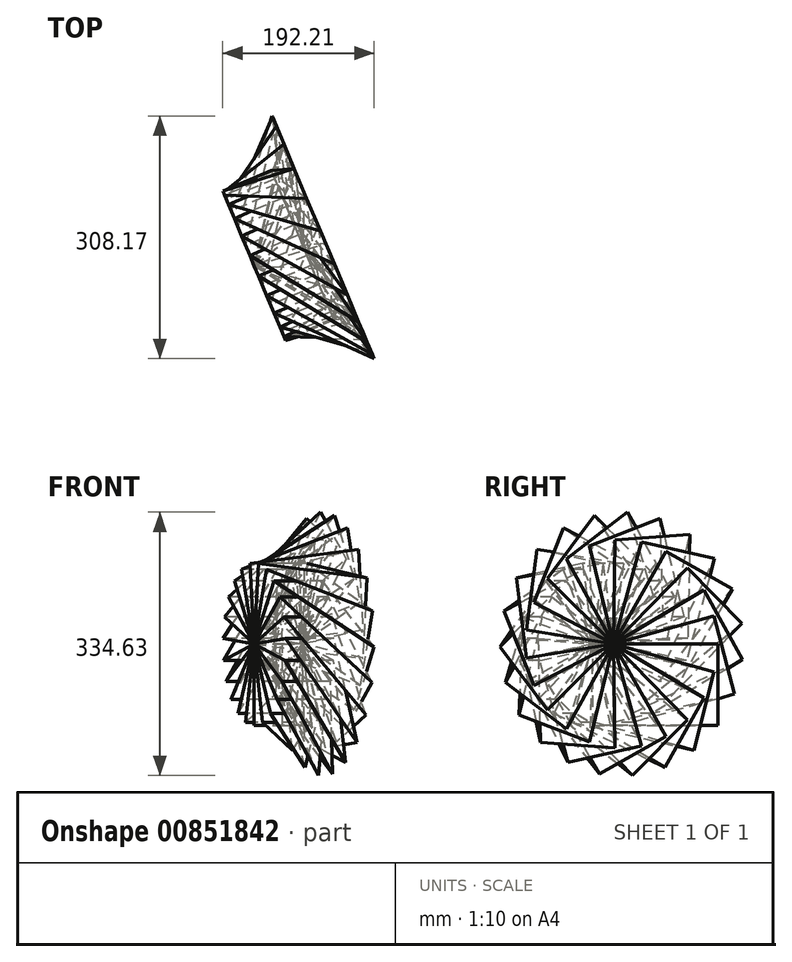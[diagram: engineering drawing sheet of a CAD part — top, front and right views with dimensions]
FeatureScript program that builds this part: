
annotation { "Feature Type Name" : "Feature", "Feature Type Description" : "" }
export const myFeature = defineFeature(function(context is Context, id is Id, definition is map)
    precondition{}
    {
        {
            var Q0;
            Q0=qCreatedBy(makeId("Top.planeOp"),FACE);
            var sketch = newSketch(context, id + "F0", { "sketchPlane" : qUnion([Q0])});
            skLineSegment(sketch, "E0", {"start": v(61.6, 25.9) * mm, "end": v(0, 0) * mm});
            skLineSegment(sketch, "E1", {"start": v(0, 0) * mm, "end": v(36, 158.63) * mm});
            skLineSegment(sketch, "E2", {"start": v(36, 158.63) * mm, "end": v(61.6, 25.9) * mm});
            skSolve(sketch);
        }
        {
            var Q0;
            Q0=makeQuery(id+"F0.imprint","IMPRINT",FACE,{"disambiguationData":[TD([[makeQuery(id+"F0.imprint","IMPRINT",EDGE,{"derivedFrom":sQuery(id+"F0.wireOp",EDGE,"E0")}),-1.0]])]});
            extrude(context, id + "F1", {"entities" : qUnion([Q0]), "oppositeDirection" : true, "depth" : 103.17 * mm, "offsetDistance" : 25.4 * mm});
        }
        {
            var Q0;
            Q0=makeQuery(id+"F1.opExtrude","SWEPT_BODY",BODY,{"disambiguationData":[OSD([sQuery(id+"F0.wireOp",EDGE,"E0"),sQuery(id+"F0.wireOp",EDGE,"E1"),sQuery(id+"F0.wireOp",EDGE,"E2")])]});
            var Q1;
            Q1=makeQuery(id+"F1.opExtrude","CAP_EDGE",EDGE,{"disambiguationData":[OSD([sQuery(id+"F0.wireOp",EDGE,"E0")])],"isStart":true});
            circularPattern(context, id + "F2", {"entities" : qUnion([Q0]), "axis" : qUnion([Q1]), "angle" : 360 * degree, "instanceCount" : 23, "equalSpace" : true});
        }
    });
